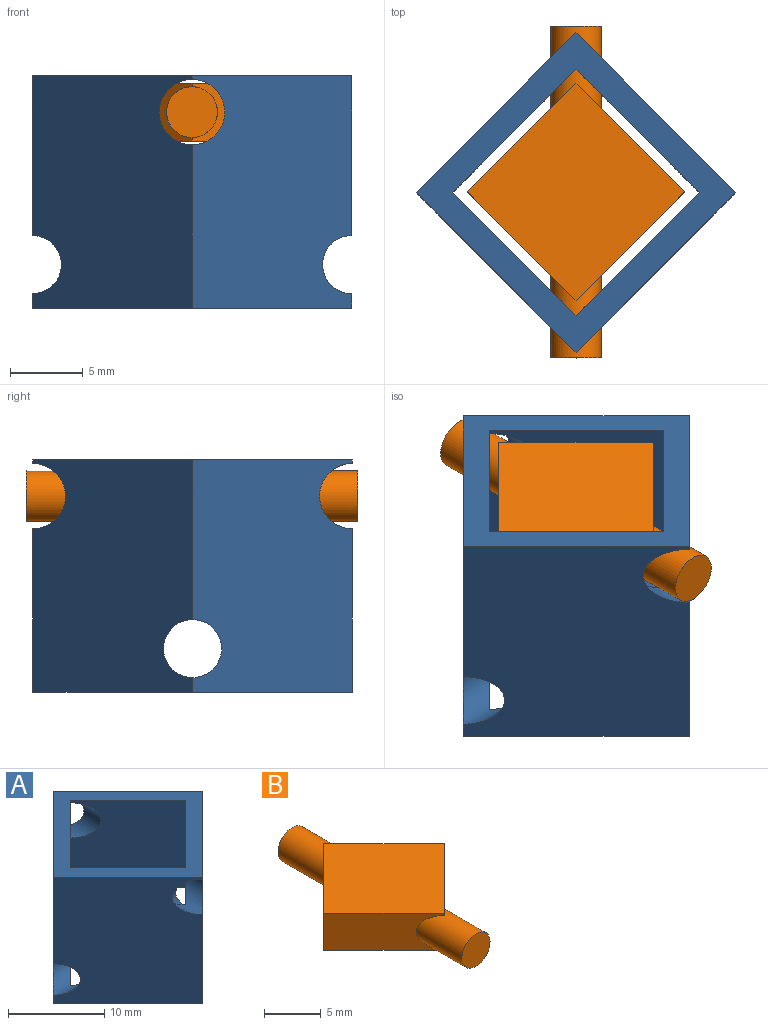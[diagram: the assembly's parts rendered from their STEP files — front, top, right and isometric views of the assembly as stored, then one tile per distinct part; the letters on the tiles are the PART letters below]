
ASSEMBLY  parts=2 mates=1
PART A: 14 faces, bbox 22x22x16 mm
  f0: plane 16x8.5mm, normal (-0.71,-0.71,0), area 172.2mm2, adj f1,f7,f8,f9,f10,f13
  f1: plane 16x8.5mm, normal (-0.71,0.71,0), area 172.2mm2, adj f0,f2,f8,f9,f11,f13
  f2: plane 16x8.5mm, normal (0.71,0.71,0), area 172.2mm2, adj f1,f7,f8,f9,f11,f12
  f3: plane 16x11mm, normal (0.71,-0.71,0), area 228.8mm2, adj f4,f6,f8,f9,f11,f13
  f4: plane 16x11mm, normal (0.71,0.71,0), area 228.8mm2, adj f3,f5,f8,f9,f10,f13
  f5: plane 16x11mm, normal (-0.71,0.71,0), area 228.8mm2, adj f4,f6,f8,f9,f10,f12
  f6: plane 16x11mm, normal (-0.71,-0.71,0), area 228.8mm2, adj f3,f5,f8,f9,f11,f12
  f7: plane 16x8.5mm, normal (0.71,-0.71,0), area 172.2mm2, adj f0,f2,f8,f9,f10,f12
  f8: plane 22x22mm, normal (0,0,1), area 97.5mm2, adj f0,f1,f2,f3,f4,f5,f6,f7
  f9: plane 22x22mm, normal (0,0,-1), area 97.5mm2, adj f0,f1,f2,f3,f4,f5,f6,f7
  f10: cylinder r=2.25mm len=4.76mm, axis (0,-1,0), area 35.3mm2, adj f0,f4,f5,f7
  f11: cylinder r=2.25mm len=4.76mm, axis (0,-1,0), area 35.3mm2, adj f1,f2,f3,f6
  f12: cylinder r=2mm len=4.51mm, axis (1,0,0), area 31.4mm2, adj f2,f5,f6,f7
  f13: cylinder r=2mm len=4.51mm, axis (1,0,0), area 31.4mm2, adj f0,f1,f3,f4
PART B: 12 faces, bbox 15x22.9x4 mm
  f0: plane 7.5x7.5mm, normal (0.71,-0.71,0), area 32.2mm2, adj f1,f3,f4,f5,f7,f11
  f1: plane 7.5x7.5mm, normal (0.71,0.71,0), area 32.2mm2, adj f0,f2,f4,f5,f8,f11
  f2: plane 7.5x7.5mm, normal (-0.71,0.71,0), area 35.6mm2, adj f1,f3,f4,f5,f8
  f3: plane 7.5x7.5mm, normal (-0.71,-0.71,0), area 35.6mm2, adj f0,f2,f4,f5,f7
  f4: plane 15x15mm, normal (0,0,1), area 112.5mm2, adj f0,f1,f2,f3
  f5: plane 15x15mm, normal (0,0,-1), area 112.5mm2, adj f0,f1,f2,f3
  f6: plane 3.5x3.5mm, normal (0,-1,0), area 9.6mm2, adj f7
  f7: cylinder r=1.75mm len=5.69mm, axis (0,1,0), area 55.5mm2, adj f0,f3,f6
  f8: cylinder r=1.75mm len=5.69mm, axis (0,1,0), area 55.5mm2, adj f1,f2,f9
  f9: plane 3.5x3.5mm, normal (0,1,0), area 9.6mm2, adj f8
  f10: plane 2.5x2.5mm, normal (1,0,0), area 4.9mm2, adj f11
  f11: cylinder r=1.25mm len=12.7mm, axis (-1,0,0), area 93.5mm2, adj f0,f1,f10
PLACE A t=(10.6,5.8,7.75)mm
PLACE B t=(10.6,5.84,15.25)mm
MATE cylindrical B.f7 <-> A.f10  axis (0,1,0) through (10.6,-5.59,15.25)mm
